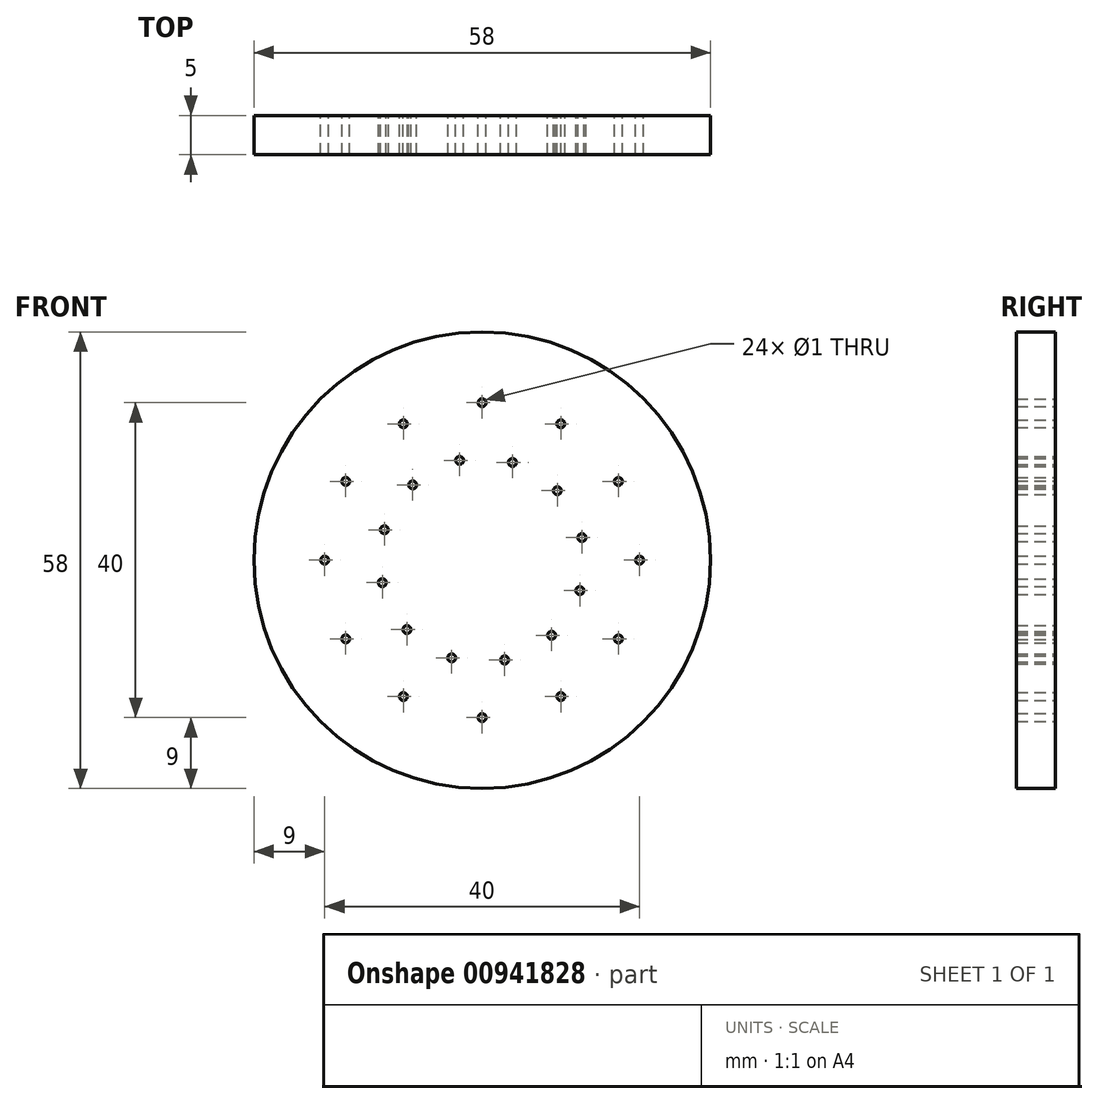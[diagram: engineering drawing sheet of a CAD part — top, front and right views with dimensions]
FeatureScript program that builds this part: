
annotation { "Feature Type Name" : "Feature", "Feature Type Description" : "" }
export const myFeature = defineFeature(function(context is Context, id is Id, definition is map)
    precondition{}
    {
        {
            var Q0;
            Q0=qCreatedBy(makeId("Front.planeOp"),FACE);
            var sketch = newSketch(context, id + "F0", { "sketchPlane" : qUnion([Q0])});
            skCircle(sketch, "E0", {"center": v(0, 0) * mm, "radius": 29 * mm});
            skCircle(sketch, "E1", {"center": v(0, 20) * mm, "radius": 0.5 * mm});
            skCircle(sketch, "E2", {"center": v(3.86, 12.41) * mm, "radius": 0.5 * mm});
            skCircle(sketch, "E3.1.0", {"center": v(-10, 17.32) * mm, "radius": 0.5 * mm});
            skCircle(sketch, "E3.1.1", {"center": v(-2.86, 12.68) * mm, "radius": 0.5 * mm});
            skCircle(sketch, "E3.2.0", {"center": v(-17.32, 10) * mm, "radius": 0.5 * mm});
            skCircle(sketch, "E3.2.1", {"center": v(-8.82, 9.55) * mm, "radius": 0.5 * mm});
            skCircle(sketch, "E3.3.0", {"center": v(-20, 0) * mm, "radius": 0.5 * mm});
            skCircle(sketch, "E3.3.1", {"center": v(-12.41, 3.86) * mm, "radius": 0.5 * mm});
            skCircle(sketch, "E3.4.0", {"center": v(-17.32, -10) * mm, "radius": 0.5 * mm});
            skCircle(sketch, "E3.4.1", {"center": v(-12.68, -2.86) * mm, "radius": 0.5 * mm});
            skCircle(sketch, "E3.5.0", {"center": v(-10, -17.32) * mm, "radius": 0.5 * mm});
            skCircle(sketch, "E3.5.1", {"center": v(-9.55, -8.82) * mm, "radius": 0.5 * mm});
            skCircle(sketch, "E3.6.0", {"center": v(0, -20) * mm, "radius": 0.5 * mm});
            skCircle(sketch, "E3.6.1", {"center": v(-3.86, -12.41) * mm, "radius": 0.5 * mm});
            skCircle(sketch, "E3.7.0", {"center": v(10, -17.32) * mm, "radius": 0.5 * mm});
            skCircle(sketch, "E3.7.1", {"center": v(2.86, -12.68) * mm, "radius": 0.5 * mm});
            skCircle(sketch, "E3.8.0", {"center": v(17.32, -10) * mm, "radius": 0.5 * mm});
            skCircle(sketch, "E3.8.1", {"center": v(8.82, -9.55) * mm, "radius": 0.5 * mm});
            skCircle(sketch, "E3.9.0", {"center": v(20, 0) * mm, "radius": 0.5 * mm});
            skCircle(sketch, "E3.9.1", {"center": v(12.41, -3.86) * mm, "radius": 0.5 * mm});
            skCircle(sketch, "E3.10.0", {"center": v(17.32, 10) * mm, "radius": 0.5 * mm});
            skCircle(sketch, "E3.10.1", {"center": v(12.68, 2.86) * mm, "radius": 0.5 * mm});
            skCircle(sketch, "E3.11.0", {"center": v(10, 17.32) * mm, "radius": 0.5 * mm});
            skCircle(sketch, "E3.11.1", {"center": v(9.55, 8.82) * mm, "radius": 0.5 * mm});
            skSolve(sketch);
        }
        {
            var Q0;
            Q0=makeQuery(id+"F0.imprint","IMPRINT",FACE,{"disambiguationData":[TD([[makeQuery(id+"F0.imprint","IMPRINT",EDGE,{"derivedFrom":sQuery(id+"F0.wireOp",EDGE,"E0")}),1.0]])]});
            extrude(context, id + "F1", {"entities" : qUnion([Q0]), "depth" : 5 * mm, "offsetDistance" : 25 * mm});
        }
    });
